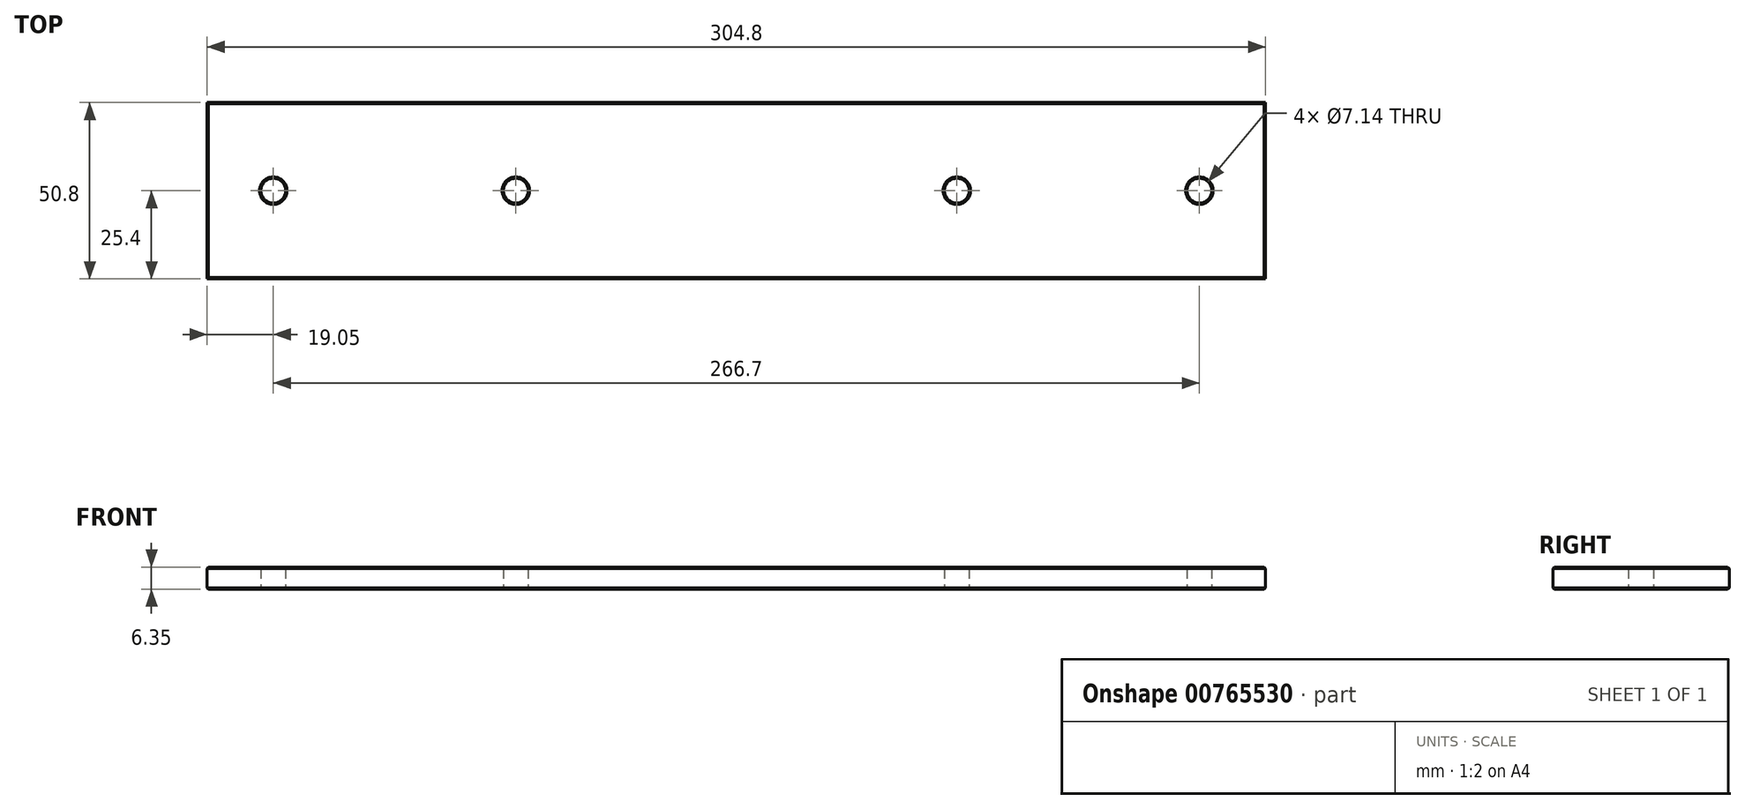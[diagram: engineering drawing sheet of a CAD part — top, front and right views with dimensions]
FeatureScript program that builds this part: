
annotation { "Feature Type Name" : "Feature", "Feature Type Description" : "" }
export const myFeature = defineFeature(function(context is Context, id is Id, definition is map)
    precondition{}
    {
        {
            var Q0;
            Q0=qCreatedBy(makeId("Top.planeOp"),FACE);
            var sketch = newSketch(context, id + "F0", { "sketchPlane" : qUnion([Q0]), "disableImprinting" : false});
            skLineSegment(sketch, "E0.bottom", {"start": v(152.4, 25.4) * mm, "end": v(-152.4, 25.4) * mm});
            skLineSegment(sketch, "E0.top", {"start": v(152.4, -25.4) * mm, "end": v(-152.4, -25.4) * mm});
            skLineSegment(sketch, "E0.left", {"start": v(152.4, 25.4) * mm, "end": v(152.4, -25.4) * mm});
            skLineSegment(sketch, "E0.right", {"start": v(-152.4, 25.4) * mm, "end": v(-152.4, -25.4) * mm});
            skPoint(sketch, "E0.middle", {"position": v(0, 0) * mm});
            skCircle(sketch, "E1", {"center": v(-133.35, 0) * mm, "radius": 3.57 * mm});
            skCircle(sketch, "E2", {"center": v(-63.5, 0) * mm, "radius": 3.57 * mm});
            skCircle(sketch, "E3", {"center": v(63.5, 0) * mm, "radius": 3.57 * mm});
            skCircle(sketch, "E4", {"center": v(133.35, 0) * mm, "radius": 3.57 * mm});
            skLineSegment(sketch, "E5", {"start": v(-133.35, 0) * mm, "end": v(-152.4, 0) * mm, "construction": true});
            skLineSegment(sketch, "E6", {"start": v(-63.5, 0) * mm, "end": v(63.5, 0) * mm, "construction": true});
            skSolve(sketch);
        }
        {
            var Q0;
            Q0=makeQuery(id+"F0.imprint","IMPRINT",FACE,{"disambiguationData":[TD([[makeQuery(id+"F0.imprint","IMPRINT",EDGE,{"derivedFrom":sQuery(id+"F0.wireOp",EDGE,"E0.bottom")}),1.0]])]});
            var Q1;
            Q1=sQuery(id+"F0.wireOp",EDGE,"E0.bottom");
            var Q2;
            Q2=sQuery(id+"F0.wireOp",EDGE,"E0.top");
            var Q3;
            Q3=sQuery(id+"F0.wireOp",EDGE,"E0.left");
            var Q4;
            Q4=sQuery(id+"F0.wireOp",EDGE,"E0.right");
            extrude(context, id + "F1", {"entities" : qUnion([Q0]), "surfaceEntities" : qUnion([Q1, Q2, Q3, Q4]), "depth" : 6.35 * mm, "offsetDistance" : 25.4 * mm});
        }
        {
            var Q0;
            Q0=makeQuery(id+"F1.opExtrude","CAP_FACE",FACE,{"disambiguationData":[OSD([sQuery(id+"F0.wireOp",EDGE,"E0.bottom"),sQuery(id+"F0.wireOp",EDGE,"E0.top"),sQuery(id+"F0.wireOp",EDGE,"E0.left"),sQuery(id+"F0.wireOp",EDGE,"E0.right"),sQuery(id+"F0.wireOp",EDGE,"E1"),sQuery(id+"F0.wireOp",EDGE,"E2"),sQuery(id+"F0.wireOp",EDGE,"E3"),sQuery(id+"F0.wireOp",EDGE,"E4")])],"isStart":true});
            var Q1;
            Q1=makeQuery(id+"F1.opExtrude","CAP_EDGE",EDGE,{"disambiguationData":[OSD([sQuery(id+"F0.wireOp",EDGE,"E0.bottom")])],"isStart":false});
            var Q2;
            Q2=makeQuery(id+"F1.opExtrude","CAP_FACE",FACE,{"disambiguationData":[OSD([sQuery(id+"F0.wireOp",EDGE,"E0.bottom"),sQuery(id+"F0.wireOp",EDGE,"E0.top"),sQuery(id+"F0.wireOp",EDGE,"E0.left"),sQuery(id+"F0.wireOp",EDGE,"E0.right"),sQuery(id+"F0.wireOp",EDGE,"E1"),sQuery(id+"F0.wireOp",EDGE,"E2"),sQuery(id+"F0.wireOp",EDGE,"E3"),sQuery(id+"F0.wireOp",EDGE,"E4")])],"isStart":false});
            chamfer(context, id + "F2", {"entities" : qUnion([Q0, Q1, Q2]), "width" : 0.4 * mm, "tangentPropagation" : true});
        }
    });
